# Revit family: QF_Varimixer_AR30
name_source: partatom
category: Specialty Equipment
units: mm (PartAtom-declared; Revit-internal decimal feet)

## family parameters
Always vertical = Yes
Cut with Voids When Loaded = No
OmniClass Number = 23.40.40.14.14.11
OmniClass Title = Food Mixers
Part Type = Normal
Room Calculation Point = No
Round Connector Dimension = Use Diameter
Shared = No
Work Plane-Based = No

## types (6) — shared parameters
Bowl size = 30 liter
Connected with neutral = Yes
Depth = 934 mm
Description = Planetary mixer AR30
Electrical Connection Height = 1012 mm
Height = 1209.675 mm
Homepage = https://www.varimixer.com
Ingress protection = IP32
Length = 570 mm
Manufacturer = Varimixer A/S
Model = AR30
Panel name = VL-1 (manual) or VL-1S (electrical)
Plug included = No
Product description = Planetary mixer, heavy duty for whipping, kneading and mixing
Product name = AR30
URL = www.varimixer.com
URL datasheet = https://www.varimixer.com
Weight in Pounds = 456
Weigth in kilograms = 170

## per-type parameters (varying)
| type | Cycle | Full Load Current | Horsepower | Number of Phases | Power | Voltage |
| 115V/60Hz/1Ph/USA | 60 Hz | 20 A | 2 hp | 3 | 2200 W | 115 V |
| 208V/60Hz/1Ph/USA | 60 Hz | 11 A | 2 | 1 | 2200 W | 208 V |
| 208V/60Hz/3Ph/USA | 60 Hz | 6 A | 2 | 3 | 2200 W | 208 V |
| 230V/50Hz/1Ph/Europe | 50 Hz | 12 A |  | 1 | 1500 W | 230 V |
| 400V/50Hz/3Ph/Europe | 50 Hz | 3 A |  | 3 | 1000 W | 400 V |
| Others on request | 0 Hz | 0 A | 0 | 1 | 0 W | 0 V |

## geometry (parser evidence)
native form markers: Blend x10, Sweep x5
no freeform markers — native parametric forms only
